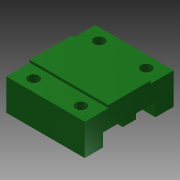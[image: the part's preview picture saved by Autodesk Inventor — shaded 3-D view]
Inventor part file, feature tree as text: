
AUTODESK INVENTOR PART (.ipt)
format: ipt  version: 2015 SP1 (Build 190203100, 203)  size: 140,800 bytes
history: native  units: mm
features: extrude x5, sketch x3, projected_geometry x2, hole x1, pattern_linear x1
ambient origin geometry x8: Origin, YZ Plane, XZ Plane, XY Plane, X Axis, Y Axis, Z Axis, Center Point
bodies: Solid1 (feature_tree)
feature tree (12):
  sketch  "Sketch1"  dims[d0=34.0mm d1=30.0mm]
  extrude  "Extrusion1"  Depth=30.0mm
  extrude  "Extrusion2"  Depth=16.0mm
  hole  "Hole1"  [1 undecoded]
  pattern_linear  "Rectangular Pattern1"  Spacing1=2.0mm  [1 undecoded]
  extrude  "Extrusion3"  Depth=3.0mm TaperAngle=0.0deg
  sketch  "Sketch3"  dims[d4=6.0mm d5=4.5mm d6=2.0mm d7=0.0mm d8=3.0mm d9=0.0mm d10=4.0mm d11=6.0mm d12=4.0mm d13=2.0mm d14=90.0deg d15=8.0mm d16=20.594885mm d17=20.0mm d19=18.0mm d20=20.0mm d22=25.0mm d23=5.0mm d24=0.0mm d25=5.0mm d26=2.0mm d27=0.0mm d28=20.0mm d29=5.0mm d30=0.0mm]
  extrude  "Extrusion4"  Depth=20.0mm
  extrude  "Extrusion5"  Depth=5.0mm
  sketch  "Sketch2"  dims[d2=16.0mm d3=4.0mm]
  projected_geometry  "Projected Loop1"
  projected_geometry  "Projected Loop2"
note: 2 required parameter values undecoded (feature->parameter linkage not recoverable at this tier; creation-order binding heuristic only, values carry confidence <= 0.55)
